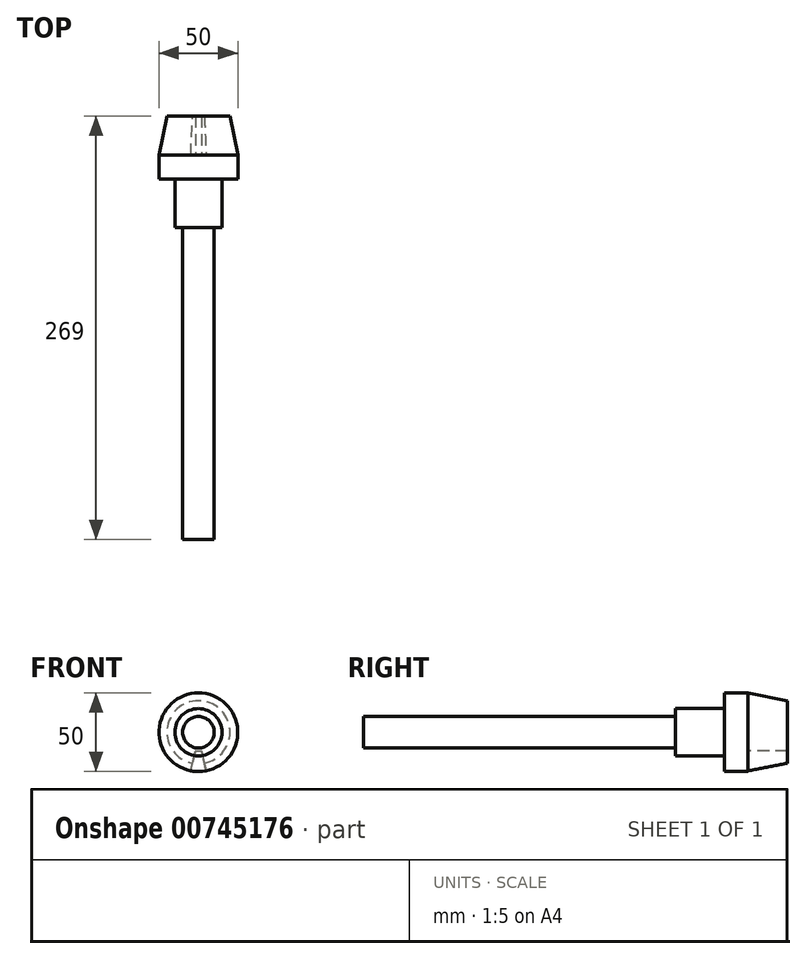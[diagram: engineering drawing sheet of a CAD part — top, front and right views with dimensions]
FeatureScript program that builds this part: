
annotation { "Feature Type Name" : "Feature", "Feature Type Description" : "" }
export const myFeature = defineFeature(function(context is Context, id is Id, definition is map)
    precondition{}
    {
        {
            var Q0;
            Q0=qCreatedBy(makeId("Front.planeOp"),FACE);
            var sketch = newSketch(context, id + "F0", { "sketchPlane" : qUnion([Q0])});
            skCircle(sketch, "E0", {"center": v(0, 0) * mm, "radius": 25 * mm});
            skSolve(sketch);
        }
        {
            var Q0;
            Q0 = qSketchRegion(id + "F0", true);
            extrude(context, id + "F1", {"entities" : qUnion([Q0]), "depth" : 40 * mm, "offsetDistance" : 25 * mm});
        }
        {
            var Q0;
            Q0=makeQuery(id+"F1.opExtrude","CAP_EDGE",EDGE,{"disambiguationData":[OSD([sQuery(id+"F0.wireOp",EDGE,"E0")])],"isStart":true});
            chamfer(context, id + "F2", {"entities" : qUnion([Q0]), "chamferType" : ChamferType.TWO_OFFSETS, "width1" : 25 * mm, "oppositeDirection" : false, "width2" : 5 * mm, "tangentPropagation" : true});
        }
        {
            var Q0;
            Q0=qCreatedBy(makeId("Front.planeOp"),FACE);
            cPlane(context, id + "F3", {"entities" : qUnion([Q0]), "cplaneType" : CPlaneType.OFFSET, "offset" : 25 * mm, "width" : 150 * mm, "height" : 150 * mm});
        }
        {
            var Q0;
            Q0=qCreatedBy(makeId("Front.planeOp"),FACE);
            var sketch = newSketch(context, id + "F4", { "sketchPlane" : qUnion([Q0])});
            skLineSegment(sketch, "E1", {"start": v(2, -12) * mm, "end": v(8, -38) * mm});
            skLineSegment(sketch, "E2", {"start": v(8, -38) * mm, "end": v(-8, -38) * mm});
            skLineSegment(sketch, "E3", {"start": v(-8, -38) * mm, "end": v(-2, -12) * mm});
            skLineSegment(sketch, "E4", {"start": v(-2, -12) * mm, "end": v(2, -12) * mm});
            skSolve(sketch);
        }
        {
            var Q0;
            Q0=qCreatedBy(id+"F3.planeOp",FACE);
            var sketch = newSketch(context, id + "F5", { "sketchPlane" : qUnion([Q0])});
            skLineSegment(sketch, "E5", {"start": v(2, -12) * mm, "end": v(-2, -12) * mm});
            skLineSegment(sketch, "E6", {"start": v(-2, -12) * mm, "end": v(-8, -38) * mm});
            skLineSegment(sketch, "E7", {"start": v(-8, -38) * mm, "end": v(8, -38) * mm});
            skLineSegment(sketch, "E8", {"start": v(8, -38) * mm, "end": v(2, -12) * mm});
            skSolve(sketch);
        }
        {
            var Q0;
            Q0=qCreatedBy(makeId("Top.planeOp"),FACE);
            var sketch = newSketch(context, id + "F6", { "sketchPlane" : qUnion([Q0])});
            skLineSegment(sketch, "E9", {"start": v(0, 0) * mm, "end": v(0, -65) * mm, "construction": true});
            skSolve(sketch);
        }
        {
            var Q1;
            Q1 = qSketchRegion(id + "F4", true);
            var Q2;
            Q2 = qSketchRegion(id + "F5", true);
            loft(context, id + "F7", {"operationType" : NewBodyOperationType.REMOVE, "sheetProfilesArray" : [{ "sheetProfileEntities" : qUnion([Q1]) }, { "sheetProfileEntities" : qUnion([Q2]) }]});
        }
        {
            var Q0;
            Q0=makeQuery(id+"F1.opExtrude","CAP_FACE",FACE,{"disambiguationData":[OSD([sQuery(id+"F0.wireOp",EDGE,"E0")])],"isStart":false});
            var sketch = newSketch(context, id + "F8", { "sketchPlane" : qUnion([Q0])});
            skCircle(sketch, "E10", {"center": v(0, 0) * mm, "radius": 15 * mm});
            skSolve(sketch);
        }
        {
            var Q0;
            Q0 = qSketchRegion(id + "F8", true);
            extrude(context, id + "F9", {"entities" : qUnion([Q0]), "operationType" : NewBodyOperationType.ADD, "depth" : 31 * mm, "offsetDistance" : 25 * mm});
        }
        {
            var Q0;
            Q0=makeQuery(id+"F9.opExtrude","CAP_FACE",FACE,{"disambiguationData":[OSD([sQuery(id+"F8.wireOp",EDGE,"E10")])],"isStart":false});
            var sketch = newSketch(context, id + "F10", { "sketchPlane" : qUnion([Q0])});
            skCircle(sketch, "E11", {"center": v(0, 0) * mm, "radius": 10 * mm});
            skSolve(sketch);
        }
        {
            var Q0;
            Q0 = qSketchRegion(id + "F10", true);
            extrude(context, id + "F11", {"entities" : qUnion([Q0]), "operationType" : NewBodyOperationType.ADD, "depth" : 198 * mm, "offsetDistance" : 25 * mm});
        }
    });
